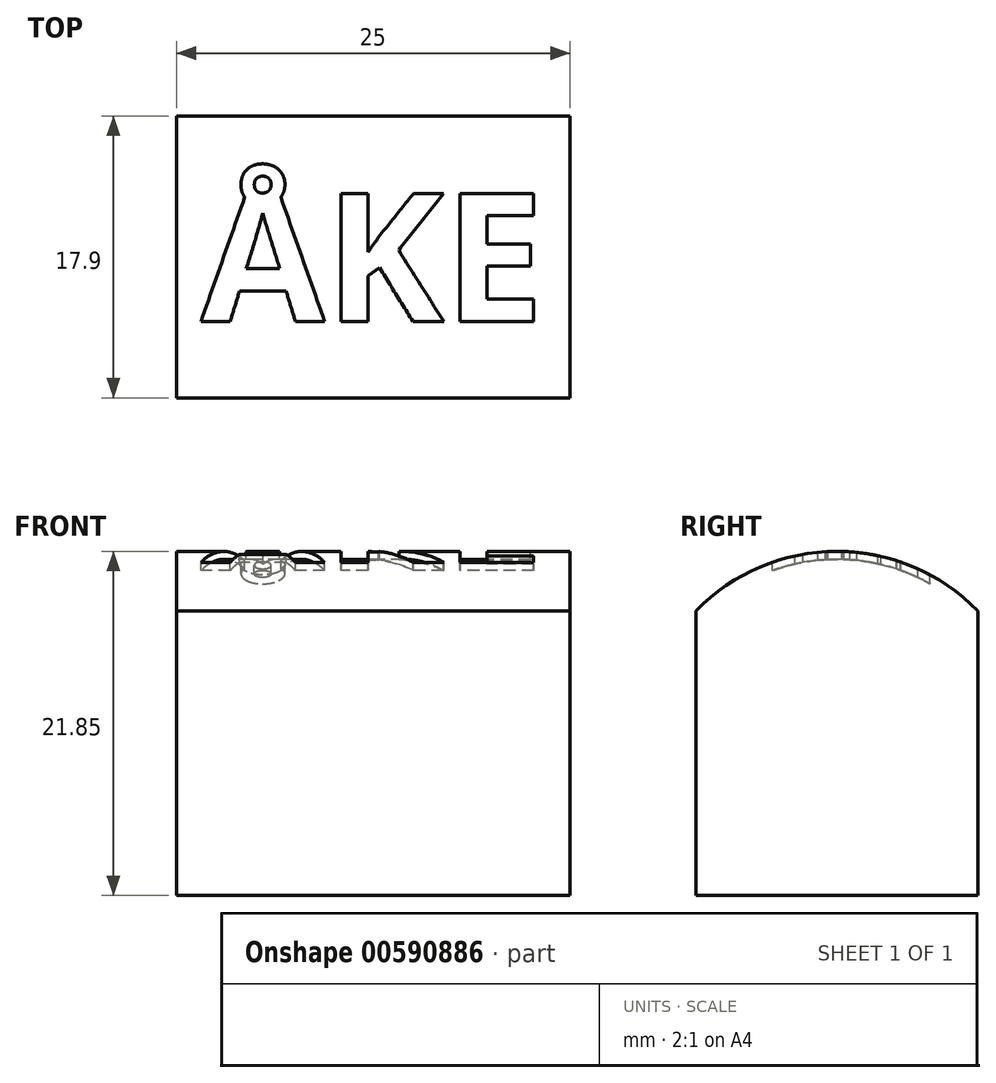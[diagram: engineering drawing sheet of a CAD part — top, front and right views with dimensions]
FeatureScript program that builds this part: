
annotation { "Feature Type Name" : "Feature", "Feature Type Description" : "" }
export const myFeature = defineFeature(function(context is Context, id is Id, definition is map)
    precondition{}
    {
        {
            var Q0;
            Q0=qCreatedBy(makeId("Right.planeOp"),FACE);
            var sketch = newSketch(context, id + "F0", { "sketchPlane" : qUnion([Q0])});
            skCircle(sketch, "E0", {"center": v(0, 0) * mm, "radius": 12.5 * mm});
            skSolve(sketch);
        }
        {
            var Q0;
            Q0 = qSketchRegion(id + "F0", true);
            extrude(context, id + "F1", {"entities" : qUnion([Q0]), "depth" : 25 * mm, "offsetDistance" : 25 * mm});
        }
        {
            var Q0;
            Q0=qCreatedBy(makeId("Right.planeOp"),FACE);
            var sketch = newSketch(context, id + "F2", { "sketchPlane" : qUnion([Q0])});
            skLineSegment(sketch, "E1.top", {"start": v(-8.95, -9.35) * mm, "end": v(8.95, -9.35) * mm});
            skLineSegment(sketch, "E1.left", {"start": v(-8.95, 8.73) * mm, "end": v(-8.95, -9.35) * mm});
            skLineSegment(sketch, "E1.right", {"start": v(8.95, 8.73) * mm, "end": v(8.95, -9.35) * mm});
            skArc(sketch, "E2", {"start": v(8.95, 8.73) * mm, "mid": v(0, 12.5) * mm, "end": v(-8.95, 8.73) * mm});
            skLineSegment(sketch, "E3", {"start": v(0, -9.35) * mm, "end": v(0, 12.5) * mm, "construction": true});
            skSolve(sketch);
        }
        {
            var Q0;
            Q0 = qSketchRegion(id + "F2", true);
            extrude(context, id + "F3", {"entities" : qUnion([Q0]), "depth" : 25 * mm, "offsetDistance" : 25 * mm});
        }
        {
            var Q0;
            Q0=qCreatedBy(makeId("Top.planeOp"),FACE);
            cPlane(context, id + "F4", {"entities" : qUnion([Q0]), "cplaneType" : CPlaneType.OFFSET, "offset" : 20 * mm, "width" : 150 * mm, "height" : 150 * mm});
        }
        {
            var Q0;
            Q0=qCreatedBy(id+"F4.planeOp",FACE);
            var sketch = newSketch(context, id + "F5", { "sketchPlane" : qUnion([Q0])});
            skText(sketch, "E4", { "text": "ÅKE", "fontName": "OpenSans-Bold.ttf"});
            skLineSegment(sketch, "E5", {"start": v(23.44, 0) * mm, "end": v(1.56, 0) * mm, "construction": true});
            const initialGuessF5  = {"E4": [0.00156, -0.0041, 1, 0, 0.0082]};
            skSetInitialGuess(sketch, initialGuessF5);
            skSolve(sketch);
        }
        {
            var Q0;
            Q0 = qSketchRegion(id + "F5", true);
            var Q1;
            Q1=qCreatedBy(makeId("Top.planeOp"),FACE);
            extrude(context, id + "F6", {"entities" : qUnion([Q0]), "endBound" : BoundingType.UP_TO_SURFACE, "oppositeDirection" : true, "depth" : 1.5 * mm, "endBoundEntityFace" : qUnion([Q1]), "offsetDistance" : 25 * mm});
        }
        {
            var Q0;
            Q0=makeQuery(id+"F3.opExtrude","SWEPT_BODY",BODY,{"disambiguationData":[OSD([sQuery(id+"F2.wireOp",EDGE,"E1.top"),sQuery(id+"F2.wireOp",EDGE,"E1.left"),sQuery(id+"F2.wireOp",EDGE,"E1.right"),sQuery(id+"F2.wireOp",EDGE,"E2")])]});
            var Q1;
            Q1=makeQuery(id+"F6.opExtrude","SWEPT_BODY",BODY,{"disambiguationData":[OSD([sQuery(id+"F5.wireOp",EDGE,"E4.sketch_text.stroke-0"),sQuery(id+"F5.wireOp",EDGE,"E4.sketch_text.stroke-1"),sQuery(id+"F5.wireOp",EDGE,"E4.sketch_text.stroke-2"),sQuery(id+"F5.wireOp",EDGE,"E4.sketch_text.stroke-3"),sQuery(id+"F5.wireOp",EDGE,"E4.sketch_text.stroke-4"),sQuery(id+"F5.wireOp",EDGE,"E4.sketch_text.stroke-6"),sQuery(id+"F5.wireOp",EDGE,"E4.sketch_text.stroke-7"),sQuery(id+"F5.wireOp",EDGE,"E4.sketch_text.stroke-8"),sQuery(id+"F5.wireOp",EDGE,"E4.sketch_text.stroke-9"),sQuery(id+"F5.wireOp",EDGE,"E4.sketch_text.stroke-10"),sQuery(id+"F5.wireOp",EDGE,"E4.sketch_text.stroke-11"),sQuery(id+"F5.wireOp",EDGE,"E4.sketch_text.stroke-12"),sQuery(id+"F5.wireOp",EDGE,"E4.sketch_text.stroke-15"),sQuery(id+"F5.wireOp",EDGE,"E4.sketch_text.stroke-16"),sQuery(id+"F5.wireOp",EDGE,"E4.sketch_text.stroke-17"),sQuery(id+"F5.wireOp",EDGE,"E4.sketch_text.stroke-18"),sQuery(id+"F5.wireOp",EDGE,"E4.sketch_text.stroke-19"),sQuery(id+"F5.wireOp",EDGE,"E4.sketch_text.stroke-20"),sQuery(id+"F5.wireOp",EDGE,"E4.sketch_text.stroke-21"),sQuery(id+"F5.wireOp",EDGE,"E4.sketch_text.stroke-22"),sQuery(id+"F5.wireOp",EDGE,"E4.sketch_text.stroke-23"),sQuery(id+"F5.wireOp",EDGE,"E4.sketch_text.stroke-24"),sQuery(id+"F5.wireOp",EDGE,"E4.sketch_text.stroke-25"),sQuery(id+"F5.wireOp",EDGE,"E4.sketch_text.stroke-26"),sQuery(id+"F5.wireOp",EDGE,"E4.sketch_text.stroke-27")])]});
            var Q2;
            Q2=makeQuery(id+"F6.opExtrude","SWEPT_BODY",BODY,{"disambiguationData":[OSD([sQuery(id+"F5.wireOp",EDGE,"E4.sketch_text.stroke-28"),sQuery(id+"F5.wireOp",EDGE,"E4.sketch_text.stroke-29"),sQuery(id+"F5.wireOp",EDGE,"E4.sketch_text.stroke-30"),sQuery(id+"F5.wireOp",EDGE,"E4.sketch_text.stroke-31"),sQuery(id+"F5.wireOp",EDGE,"E4.sketch_text.stroke-32"),sQuery(id+"F5.wireOp",EDGE,"E4.sketch_text.stroke-33"),sQuery(id+"F5.wireOp",EDGE,"E4.sketch_text.stroke-34"),sQuery(id+"F5.wireOp",EDGE,"E4.sketch_text.stroke-35"),sQuery(id+"F5.wireOp",EDGE,"E4.sketch_text.stroke-36"),sQuery(id+"F5.wireOp",EDGE,"E4.sketch_text.stroke-37"),sQuery(id+"F5.wireOp",EDGE,"E4.sketch_text.stroke-38"),sQuery(id+"F5.wireOp",EDGE,"E4.sketch_text.stroke-39"),sQuery(id+"F5.wireOp",EDGE,"E4.sketch_text.stroke-40")])]});
            var Q3;
            Q3=makeQuery(id+"F6.opExtrude","SWEPT_BODY",BODY,{"disambiguationData":[OSD([sQuery(id+"F5.wireOp",EDGE,"E4.sketch_text.stroke-41"),sQuery(id+"F5.wireOp",EDGE,"E4.sketch_text.stroke-42"),sQuery(id+"F5.wireOp",EDGE,"E4.sketch_text.stroke-43"),sQuery(id+"F5.wireOp",EDGE,"E4.sketch_text.stroke-44"),sQuery(id+"F5.wireOp",EDGE,"E4.sketch_text.stroke-45"),sQuery(id+"F5.wireOp",EDGE,"E4.sketch_text.stroke-46"),sQuery(id+"F5.wireOp",EDGE,"E4.sketch_text.stroke-47"),sQuery(id+"F5.wireOp",EDGE,"E4.sketch_text.stroke-48"),sQuery(id+"F5.wireOp",EDGE,"E4.sketch_text.stroke-49"),sQuery(id+"F5.wireOp",EDGE,"E4.sketch_text.stroke-50"),sQuery(id+"F5.wireOp",EDGE,"E4.sketch_text.stroke-51"),sQuery(id+"F5.wireOp",EDGE,"E4.sketch_text.stroke-52")])]});
            booleanBodies(context, id + "F7", {"operationType" : BooleanOperationType.SUBTRACTION, "tools" : qUnion([Q0]), "targets" : qUnion([Q1, Q2, Q3]), "offset" : true, "offsetAll" : true, "offsetDistance" : 0.5 * mm, "oppositeDirection" : true, "keepTools" : true});
        }
        {
            var Q0;
            Q0=makeQuery(id+"F6.opExtrude","SWEPT_BODY",BODY,{"disambiguationData":[OSD([sQuery(id+"F5.wireOp",EDGE,"E4.sketch_text.stroke-0"),sQuery(id+"F5.wireOp",EDGE,"E4.sketch_text.stroke-1"),sQuery(id+"F5.wireOp",EDGE,"E4.sketch_text.stroke-2"),sQuery(id+"F5.wireOp",EDGE,"E4.sketch_text.stroke-3"),sQuery(id+"F5.wireOp",EDGE,"E4.sketch_text.stroke-4"),sQuery(id+"F5.wireOp",EDGE,"E4.sketch_text.stroke-6"),sQuery(id+"F5.wireOp",EDGE,"E4.sketch_text.stroke-7"),sQuery(id+"F5.wireOp",EDGE,"E4.sketch_text.stroke-8"),sQuery(id+"F5.wireOp",EDGE,"E4.sketch_text.stroke-9"),sQuery(id+"F5.wireOp",EDGE,"E4.sketch_text.stroke-10"),sQuery(id+"F5.wireOp",EDGE,"E4.sketch_text.stroke-11"),sQuery(id+"F5.wireOp",EDGE,"E4.sketch_text.stroke-12"),sQuery(id+"F5.wireOp",EDGE,"E4.sketch_text.stroke-15"),sQuery(id+"F5.wireOp",EDGE,"E4.sketch_text.stroke-16"),sQuery(id+"F5.wireOp",EDGE,"E4.sketch_text.stroke-17"),sQuery(id+"F5.wireOp",EDGE,"E4.sketch_text.stroke-18"),sQuery(id+"F5.wireOp",EDGE,"E4.sketch_text.stroke-19"),sQuery(id+"F5.wireOp",EDGE,"E4.sketch_text.stroke-20"),sQuery(id+"F5.wireOp",EDGE,"E4.sketch_text.stroke-21"),sQuery(id+"F5.wireOp",EDGE,"E4.sketch_text.stroke-22"),sQuery(id+"F5.wireOp",EDGE,"E4.sketch_text.stroke-23"),sQuery(id+"F5.wireOp",EDGE,"E4.sketch_text.stroke-24"),sQuery(id+"F5.wireOp",EDGE,"E4.sketch_text.stroke-25"),sQuery(id+"F5.wireOp",EDGE,"E4.sketch_text.stroke-26"),sQuery(id+"F5.wireOp",EDGE,"E4.sketch_text.stroke-27")])]});
            var Q1;
            Q1=makeQuery(id+"F6.opExtrude","SWEPT_BODY",BODY,{"disambiguationData":[OSD([sQuery(id+"F5.wireOp",EDGE,"E4.sketch_text.stroke-28"),sQuery(id+"F5.wireOp",EDGE,"E4.sketch_text.stroke-29"),sQuery(id+"F5.wireOp",EDGE,"E4.sketch_text.stroke-30"),sQuery(id+"F5.wireOp",EDGE,"E4.sketch_text.stroke-31"),sQuery(id+"F5.wireOp",EDGE,"E4.sketch_text.stroke-32"),sQuery(id+"F5.wireOp",EDGE,"E4.sketch_text.stroke-33"),sQuery(id+"F5.wireOp",EDGE,"E4.sketch_text.stroke-34"),sQuery(id+"F5.wireOp",EDGE,"E4.sketch_text.stroke-35"),sQuery(id+"F5.wireOp",EDGE,"E4.sketch_text.stroke-36"),sQuery(id+"F5.wireOp",EDGE,"E4.sketch_text.stroke-37"),sQuery(id+"F5.wireOp",EDGE,"E4.sketch_text.stroke-38"),sQuery(id+"F5.wireOp",EDGE,"E4.sketch_text.stroke-39"),sQuery(id+"F5.wireOp",EDGE,"E4.sketch_text.stroke-40")])]});
            var Q2;
            Q2=makeQuery(id+"F6.opExtrude","SWEPT_BODY",BODY,{"disambiguationData":[OSD([sQuery(id+"F5.wireOp",EDGE,"E4.sketch_text.stroke-41"),sQuery(id+"F5.wireOp",EDGE,"E4.sketch_text.stroke-42"),sQuery(id+"F5.wireOp",EDGE,"E4.sketch_text.stroke-43"),sQuery(id+"F5.wireOp",EDGE,"E4.sketch_text.stroke-44"),sQuery(id+"F5.wireOp",EDGE,"E4.sketch_text.stroke-45"),sQuery(id+"F5.wireOp",EDGE,"E4.sketch_text.stroke-46"),sQuery(id+"F5.wireOp",EDGE,"E4.sketch_text.stroke-47"),sQuery(id+"F5.wireOp",EDGE,"E4.sketch_text.stroke-48"),sQuery(id+"F5.wireOp",EDGE,"E4.sketch_text.stroke-49"),sQuery(id+"F5.wireOp",EDGE,"E4.sketch_text.stroke-50"),sQuery(id+"F5.wireOp",EDGE,"E4.sketch_text.stroke-51"),sQuery(id+"F5.wireOp",EDGE,"E4.sketch_text.stroke-52")])]});
            var Q3;
            Q3=makeQuery(id+"F3.opExtrude","SWEPT_BODY",BODY,{"disambiguationData":[OSD([sQuery(id+"F2.wireOp",EDGE,"E1.top"),sQuery(id+"F2.wireOp",EDGE,"E1.left"),sQuery(id+"F2.wireOp",EDGE,"E1.right"),sQuery(id+"F2.wireOp",EDGE,"E2")])]});
            booleanBodies(context, id + "F8", {"operationType" : BooleanOperationType.SUBTRACTION, "tools" : qUnion([Q0, Q1, Q2]), "targets" : qUnion([Q3])});
        }
        {
            var Q0;
            Q0=makeQuery(id+"F1.opExtrude","SWEPT_BODY",BODY,{"disambiguationData":[OSD([sQuery(id+"F0.wireOp",EDGE,"E0")])]});
            deleteBodies(context, id + "F9", {"entities" : qUnion([Q0])});
        }
    });
